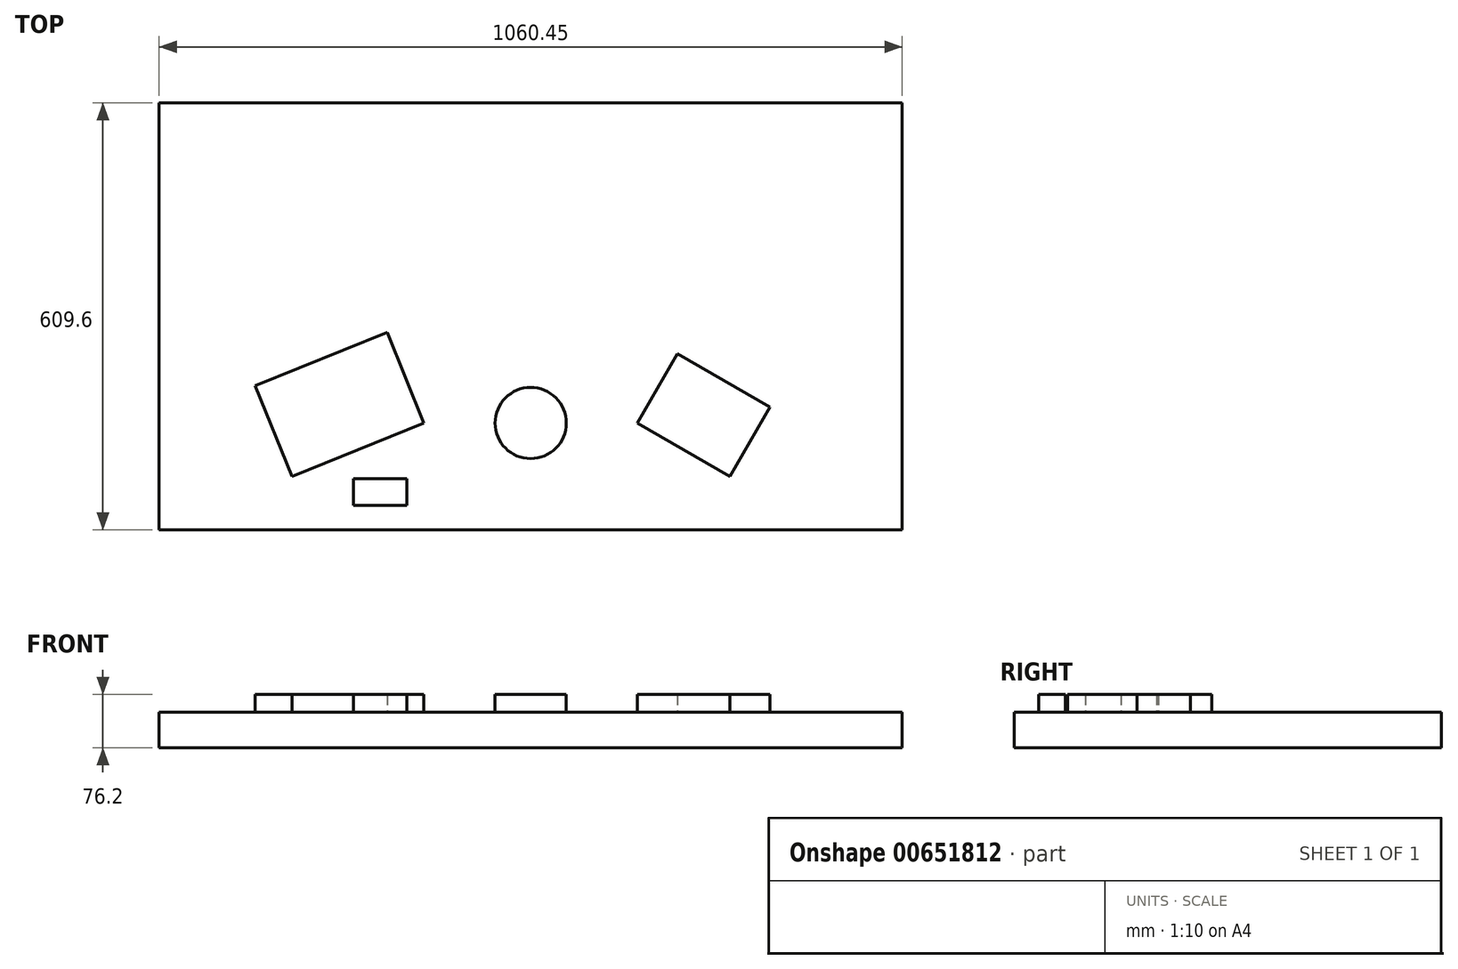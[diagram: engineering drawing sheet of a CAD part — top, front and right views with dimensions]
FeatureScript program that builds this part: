
annotation { "Feature Type Name" : "Feature", "Feature Type Description" : "" }
export const myFeature = defineFeature(function(context is Context, id is Id, definition is map)
    precondition{}
    {
        {
            var Q0;
            Q0=qCreatedBy(makeId("Top.planeOp"),FACE);
            var sketch = newSketch(context, id + "F0", { "sketchPlane" : qUnion([Q0])});
            skLineSegment(sketch, "E0.bottom", {"start": v(0, 0) * mm, "end": v(1060.45, 0) * mm});
            skLineSegment(sketch, "E0.top", {"start": v(0, 609.6) * mm, "end": v(1060.45, 609.6) * mm});
            skLineSegment(sketch, "E0.left", {"start": v(0, 0) * mm, "end": v(0, 609.6) * mm});
            skLineSegment(sketch, "E0.right", {"start": v(1060.45, 0) * mm, "end": v(1060.45, 609.6) * mm});
            skPoint(sketch, "E1", {"position": v(530.22, 0) * mm});
            skPoint(sketch, "E2", {"position": v(1060.45, 128.69) * mm});
            skPoint(sketch, "E3", {"position": v(1060.45, 306.49) * mm});
            skSolve(sketch);
        }
        {
            var Q0;
            Q0=makeQuery(id+"F0.imprint","IMPRINT",FACE,{"disambiguationData":[TD([[makeQuery(id+"F0.imprint","IMPRINT",EDGE,{"derivedFrom":sQuery(id+"F0.wireOp",EDGE,"E0.bottom")}),1.0]])]});
            var sketch = newSketch(context, id + "F1", { "sketchPlane" : qUnion([Q0])});
            skPoint(sketch, "E4", {"position": v(137.07, 205.7) * mm});
            skPoint(sketch, "E5", {"position": v(189.45, 76.2) * mm});
            skPoint(sketch, "E6", {"position": v(377.82, 152.4) * mm});
            skPoint(sketch, "E7", {"position": v(325.44, 281.9) * mm});
            skLineSegment(sketch, "E8", {"start": v(325.44, 281.9) * mm, "end": v(377.82, 152.4) * mm});
            skLineSegment(sketch, "E9", {"start": v(189.45, 76.2) * mm, "end": v(377.82, 152.4) * mm});
            skLineSegment(sketch, "E10", {"start": v(137.07, 205.7) * mm, "end": v(325.44, 281.9) * mm});
            skLineSegment(sketch, "E11", {"start": v(137.07, 205.7) * mm, "end": v(189.45, 76.2) * mm});
            skPoint(sketch, "E12", {"position": v(739.78, 251.39) * mm});
            skPoint(sketch, "E13", {"position": v(682.62, 152.4) * mm});
            skPoint(sketch, "E14", {"position": v(814.6, 76.2) * mm});
            skPoint(sketch, "E15", {"position": v(871.76, 175.19) * mm});
            skLineSegment(sketch, "E16", {"start": v(871.76, 175.19) * mm, "end": v(814.6, 76.2) * mm});
            skLineSegment(sketch, "E17", {"start": v(682.62, 152.4) * mm, "end": v(814.6, 76.2) * mm});
            skLineSegment(sketch, "E18", {"start": v(739.78, 251.39) * mm, "end": v(871.76, 175.19) * mm});
            skLineSegment(sketch, "E19", {"start": v(739.77, 251.39) * mm, "end": v(682.62, 152.4) * mm});
            skPoint(sketch, "E20", {"position": v(530.22, 152.4) * mm});
            skCircle(sketch, "E21", {"center": v(530.22, 152.4) * mm, "radius": 50.8 * mm});
            skLineSegment(sketch, "E22.bottom", {"start": v(277.29, 72.67) * mm, "end": v(353.49, 72.67) * mm});
            skLineSegment(sketch, "E22.top", {"start": v(277.29, 34.57) * mm, "end": v(353.49, 34.57) * mm});
            skLineSegment(sketch, "E22.left", {"start": v(277.29, 72.67) * mm, "end": v(277.29, 34.57) * mm});
            skLineSegment(sketch, "E22.right", {"start": v(353.49, 72.67) * mm, "end": v(353.49, 34.57) * mm});
            skSolve(sketch);
        }
        {
            var Q0;
            Q0 = qSketchRegion(id + "F0", true);
            extrude(context, id + "F2", {"entities" : qUnion([Q0]), "oppositeDirection" : true, "depth" : 50.8 * mm, "offsetDistance" : 25.4 * mm});
        }
        {
            var Q0;
            Q0 = qSketchRegion(id + "F1", true);
            extrude(context, id + "F3", {"entities" : qUnion([Q0]), "operationType" : NewBodyOperationType.ADD, "depth" : 25.4 * mm, "offsetDistance" : 25.4 * mm});
        }
    });
